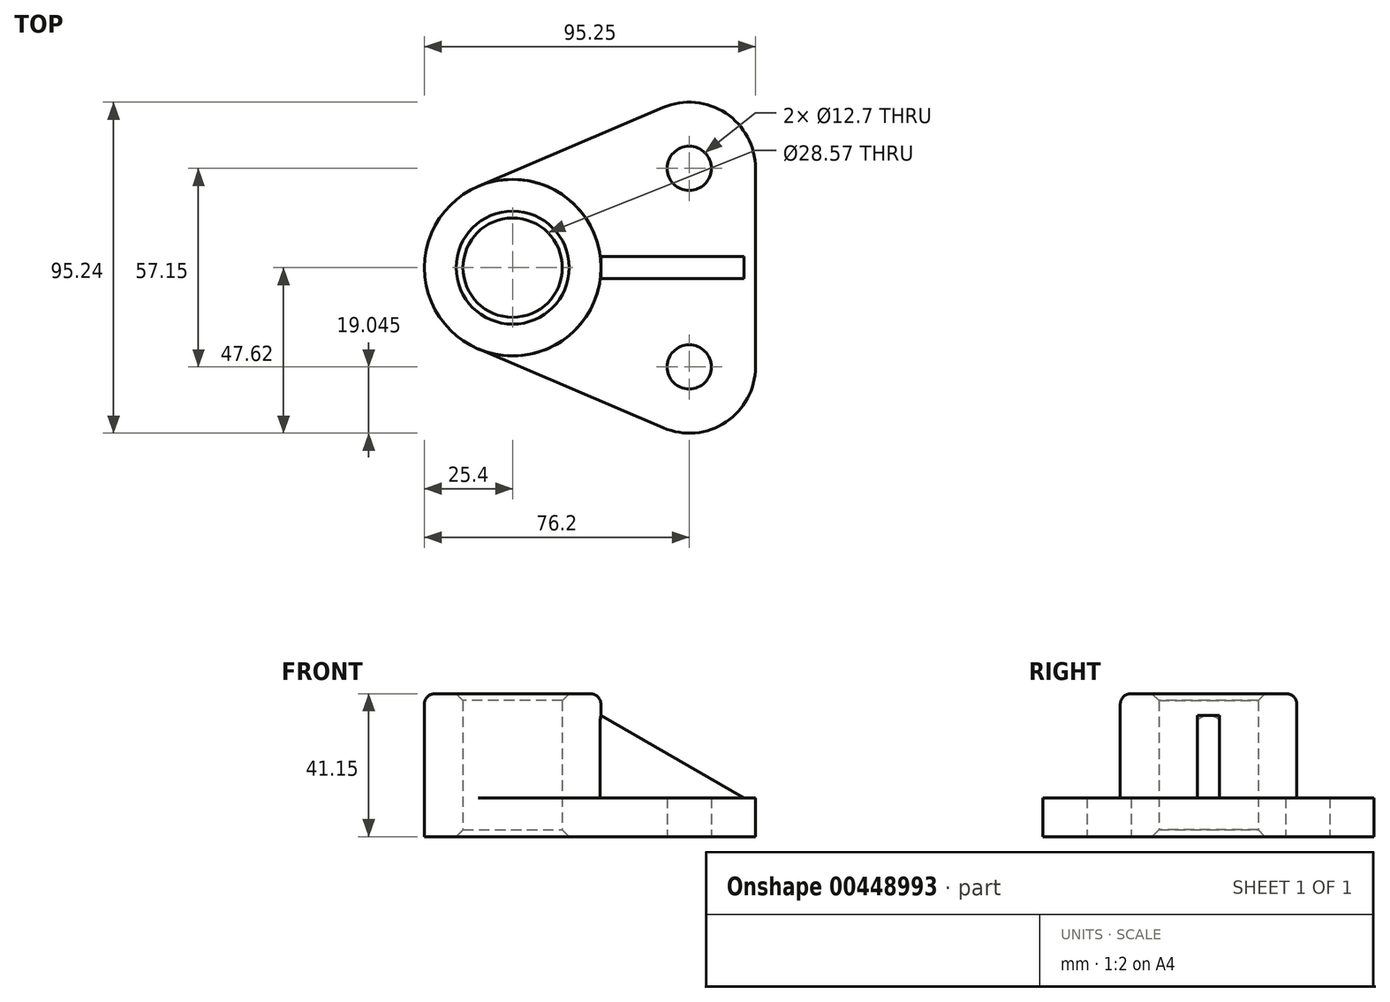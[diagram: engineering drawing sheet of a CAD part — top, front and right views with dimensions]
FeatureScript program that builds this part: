
annotation { "Feature Type Name" : "Feature", "Feature Type Description" : "" }
export const myFeature = defineFeature(function(context is Context, id is Id, definition is map)
    precondition{}
    {
        {
            var Q0;
            Q0=qCreatedBy(makeId("Top.planeOp"),FACE);
            var sketch = newSketch(context, id + "F0", { "sketchPlane" : qUnion([Q0])});
            skCircle(sketch, "E0", {"center": v(0, 0) * mm, "radius": 25.4 * mm});
            skArc(sketch, "E1", {"start": v(69.85, 28.57) * mm, "mid": v(61.3, 44.47) * mm, "end": v(43.33, 46.1) * mm});
            skArc(sketch, "E2", {"start": v(43.33, -46.1) * mm, "mid": v(61.3, -44.47) * mm, "end": v(69.85, -28.58) * mm});
            skCircle(sketch, "E3", {"center": v(0, 0) * mm, "radius": 14.29 * mm});
            skLineSegment(sketch, "E4", {"start": v(-9.97, 23.36) * mm, "end": v(43.33, 46.1) * mm});
            skLineSegment(sketch, "E5", {"start": v(-9.97, -23.36) * mm, "end": v(43.33, -46.1) * mm});
            skLineSegment(sketch, "E6", {"start": v(69.85, 28.58) * mm, "end": v(69.85, -28.58) * mm});
            skCircle(sketch, "E7", {"center": v(50.8, 28.58) * mm, "radius": 6.35 * mm});
            skCircle(sketch, "E8", {"center": v(50.8, -28.57) * mm, "radius": 6.35 * mm});
            skSolve(sketch);
        }
        {
            var Q0;
            Q0=makeQuery(id+"F0.imprint","IMPRINT",FACE,{"disambiguationData":[TD([[makeQuery(id+"F0.imprint","IMPRINT",EDGE,{"derivedFrom":sQuery(id+"F0.wireOp",EDGE,"E3")}),-1.0]])]});
            extrude(context, id + "F1", {"entities" : qUnion([Q0]), "depth" : 41.15 * mm});
        }
        {
            var Q0;
            Q0=makeQuery(id+"F0.imprint","IMPRINT",FACE,{"disambiguationData":[TD([[makeQuery(id+"F0.imprint","IMPRINT",EDGE,{"derivedFrom":sQuery(id+"F0.wireOp",EDGE,"E1")}),1.0]])]});
            extrude(context, id + "F2", {"entities" : qUnion([Q0]), "operationType" : NewBodyOperationType.ADD, "depth" : 11.18 * mm});
        }
        {
            var Q0;
            Q0=qCreatedBy(makeId("Front.planeOp"),FACE);
            var sketch = newSketch(context, id + "F3", { "sketchPlane" : qUnion([Q0])});
            skLineSegment(sketch, "E9", {"start": v(-25.4, 0) * mm, "end": v(-25.4, 41.15) * mm});
            skLineSegment(sketch, "E10", {"start": v(25.4, 41.15) * mm, "end": v(25.4, 11.18) * mm});
            skLineSegment(sketch, "E11.0", {"start": v(-14.29, 0) * mm, "end": v(14.29, 0) * mm});
            skLineSegment(sketch, "E12", {"start": v(16.26, 41.15) * mm, "end": v(14.22, 39.12) * mm});
            skLineSegment(sketch, "E13", {"start": v(14.22, 39.12) * mm, "end": v(14.22, 2.03) * mm});
            skLineSegment(sketch, "E14", {"start": v(14.22, 2.03) * mm, "end": v(16.26, 0) * mm});
            skLineSegment(sketch, "E15", {"start": v(16.26, 0) * mm, "end": v(0, 0) * mm});
            skLineSegment(sketch, "E16.0", {"start": v(-25.4, 41.15) * mm, "end": v(25.4, 41.15) * mm});
            skLineSegment(sketch, "E17", {"start": v(0, 41.15) * mm, "end": v(16.26, 41.15) * mm});
            skLineSegment(sketch, "E18", {"start": v(0, 41.15) * mm, "end": v(0, 0) * mm});
            skSolve(sketch);
        }
        {
            var Q0;
            Q0=makeQuery(id+"F3.imprint","IMPRINT",FACE,{"disambiguationData":[TD([[makeQuery(id+"F3.imprint","IMPRINT",EDGE,{"derivedFrom":sQuery(id+"F3.wireOp",EDGE,"E12")}),-1.0]])]});
            var Q1;
            Q1=sQuery(id+"F3.wireOp",EDGE,"E18");
            revolve(context, id + "F4", {"operationType" : NewBodyOperationType.REMOVE, "entities" : qUnion([Q0]), "axis" : qUnion([Q1]), "revolveType" : RevolveType.FULL, "oppositeDirection" : true});
        }
        {
            var Q0;
            Q0=qCreatedBy(makeId("Front.planeOp"),FACE);
            var sketch = newSketch(context, id + "F5", { "sketchPlane" : qUnion([Q0])});
            skLineSegment(sketch, "E19", {"start": v(-25.4, 0) * mm, "end": v(-25.4, 41.15) * mm});
            skLineSegment(sketch, "E20.0", {"start": v(69.85, 11.18) * mm, "end": v(69.85, 0) * mm});
            skLineSegment(sketch, "E21", {"start": v(25.4, 41.15) * mm, "end": v(25.4, 11.18) * mm});
            skLineSegment(sketch, "E22.0", {"start": v(43.33, 11.18) * mm, "end": v(69.85, 11.18) * mm});
            skLineSegment(sketch, "E23", {"start": v(25.4, 34.93) * mm, "end": v(66.55, 11.18) * mm});
            skLineSegment(sketch, "E24", {"start": v(25.4, 34.93) * mm, "end": v(21.65, 8.58) * mm});
            skLineSegment(sketch, "E25", {"start": v(21.65, 8.58) * mm, "end": v(66.55, 11.18) * mm});
            skSolve(sketch);
        }
        {
            var Q0;
            Q0=makeQuery(id+"F5.imprint","IMPRINT",FACE,{"disambiguationData":[TD([[makeQuery(id+"F5.imprint","IMPRINT",EDGE,{"derivedFrom":sQuery(id+"F5.wireOp",EDGE,"E23")}),-1.0]])]});
            extrude(context, id + "F6", {"entities" : qUnion([Q0]), "operationType" : NewBodyOperationType.ADD, "endBound" : BoundingType.SYMMETRIC, "depth" : 6.35 * mm});
        }
        {
            var Q0;
            Q0=makeQuery(id+"F1.opExtrude","CAP_EDGE",EDGE,{"disambiguationData":[OSD([sQuery(id+"F0.wireOp",EDGE,"E0")])],"isStart":false});
            fillet(context, id + "F7", {"entities" : qUnion([Q0]), "radius" : 3.05 * mm, "tangentPropagation" : true, "allowEdgeOverflow" : false});
        }
    });
